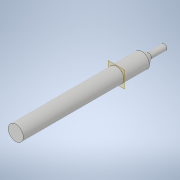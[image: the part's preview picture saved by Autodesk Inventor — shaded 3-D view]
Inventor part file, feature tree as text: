
AUTODESK INVENTOR PART (.ipt)
format: ipt  version: 2020.3 (Build 243373000, 373)  size: 125,952 bytes
history: native  units: mm
features: sketch x2, revolve x1, extrude x1, plane x1, split x1
ambient origin geometry x8: Origin, YZ Plane, XZ Plane, XY Plane, X Axis, Y Axis, Z Axis, Center Point
bodies: Solid2 (feature_tree), Solid3 (feature_tree), Solid4 (feature_tree)
feature tree (6):
  revolve  "Revolution2"  [1 undecoded]
  extrude  "Extrusion1"  Depth=50.0mm
  plane  "Work Plane1"
  split  "Split1"
  sketch  "Sketch1"  dims[d17=5.5mm d22=15.5mm]
  sketch  "Sketch2"  dims[d23=21.816616mm d24=5.0mm d25=13.613568mm d27=11.0mm d28=45.156946mm d29=90.0deg d30=15.0mm d31=30.0mm d32=250.0mm d33=0.0mm d34=50.0mm]
note: 1 required parameter value undecoded (feature->parameter linkage not recoverable at this tier; creation-order binding heuristic only, values carry confidence <= 0.55)
